# Revit family: Lighting_Outside_Focus-Lighting_Yoyo-Outdoor---1
name_source: partatom
category: Lighting Fixtures
units: mm (PartAtom-declared; Revit-internal decimal feet)

## family parameters
Cut with Voids When Loaded = No
Host = Face
Light Source = Yes
Maintain Annotation Orientation = No
OmniClass Number = 23.80.70.11
OmniClass Title = Luminaries for Internal Lighting
Part Type = Normal
Room Calculation Point = No
Round Connector Dimension = Use Diameter
Shared = No

## types (1)
- Yoyo Outdoor - 3000 - 350mm
    Apparent Load = 16 VA
    Color Filter = 16777215
    Default Elevation = 1219 mm
    Description = Yoyo is a range of elegant interior light fixtures
with low height.
    Diameter = 350 mm  [stored 1.14829 ft]
    Dimming Lamp Color Temperature Shift = <None>
    Emit Shape Visible in Rendering = No
    Emit from Circle Diameter = 298 mm  [stored 0.97769 ft]
    Height = 51 mm
    Installation Type = Ceiling or Wall Mounted
    Lamp = LED
    Lens Material = Focus-Lighting - Acrylic - LED
    Manufacturer = Focus-Lighting
    Model = Yoyo Outdoor
    Number of Poles = 1
    Photometric File Name = yoyo-350-500ma-16w-3000k-cri90-cdp-prismatisk.ies
    Photometric Web File = Generic Default - Select File (Matching Photometric File Name)
    Power Factor = 1
    Product Documentation Link = https://www.focus-lighting.dk
    Product Material = Focus-Lighting - Metal - Cast Aluminium
    Product Page URL = https://www.focus-lighting.dk
    Product data url = https://www.bimobject.com
    Tilt Angle = -90.00°
    URL = https://www.focus-lighting.dk
    Version = 1
    Voltage = 220 V
    Watts = 16 W
    Weight - Mass = 2.10 kg

note: [stored X ft] marks values corroborated as IEEE doubles in the binary element streams (Revit-internal decimal feet)

## geometry (parser evidence)
native form markers: Sweep x1
no freeform markers — native parametric forms only
